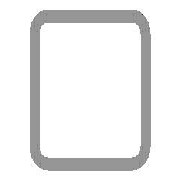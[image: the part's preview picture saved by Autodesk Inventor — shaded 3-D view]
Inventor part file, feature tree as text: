
AUTODESK INVENTOR PART (.ipt)
format: ipt  version: 2025 (Build 290162010, 162A)  size: 133,120 bytes
history: native  units: mm (DEFAULTED — no unit token found)
features: other x4, sketch x1, plane x1
ambient origin geometry x8: Origin, YZ Plane, XZ Plane, XY Plane, X Axis, Y Axis, Z Axis, Center Point
bodies: Solid1 (feature_tree), Body (feature_tree)
feature tree (6):
  parser-record x1  (decoder bookkeeping rows leaked as tree rows — omitted from the tree; the rows remain in map.json)
  other  "Driven Length"
  other  "Start Plane"
  other  "End Plane"
  sketch  "Sketch3"  dims[d3=6340.0mm d4=0.0mm d7=6.0mm d9=80.0mm d11=80.0mm d12=3.0mm d13=80.0mm d14=6420.0mm d15=40.0mm d16=40.0mm d17=90.0deg d18=6340.0mm]
  plane  "Work Plane3"
